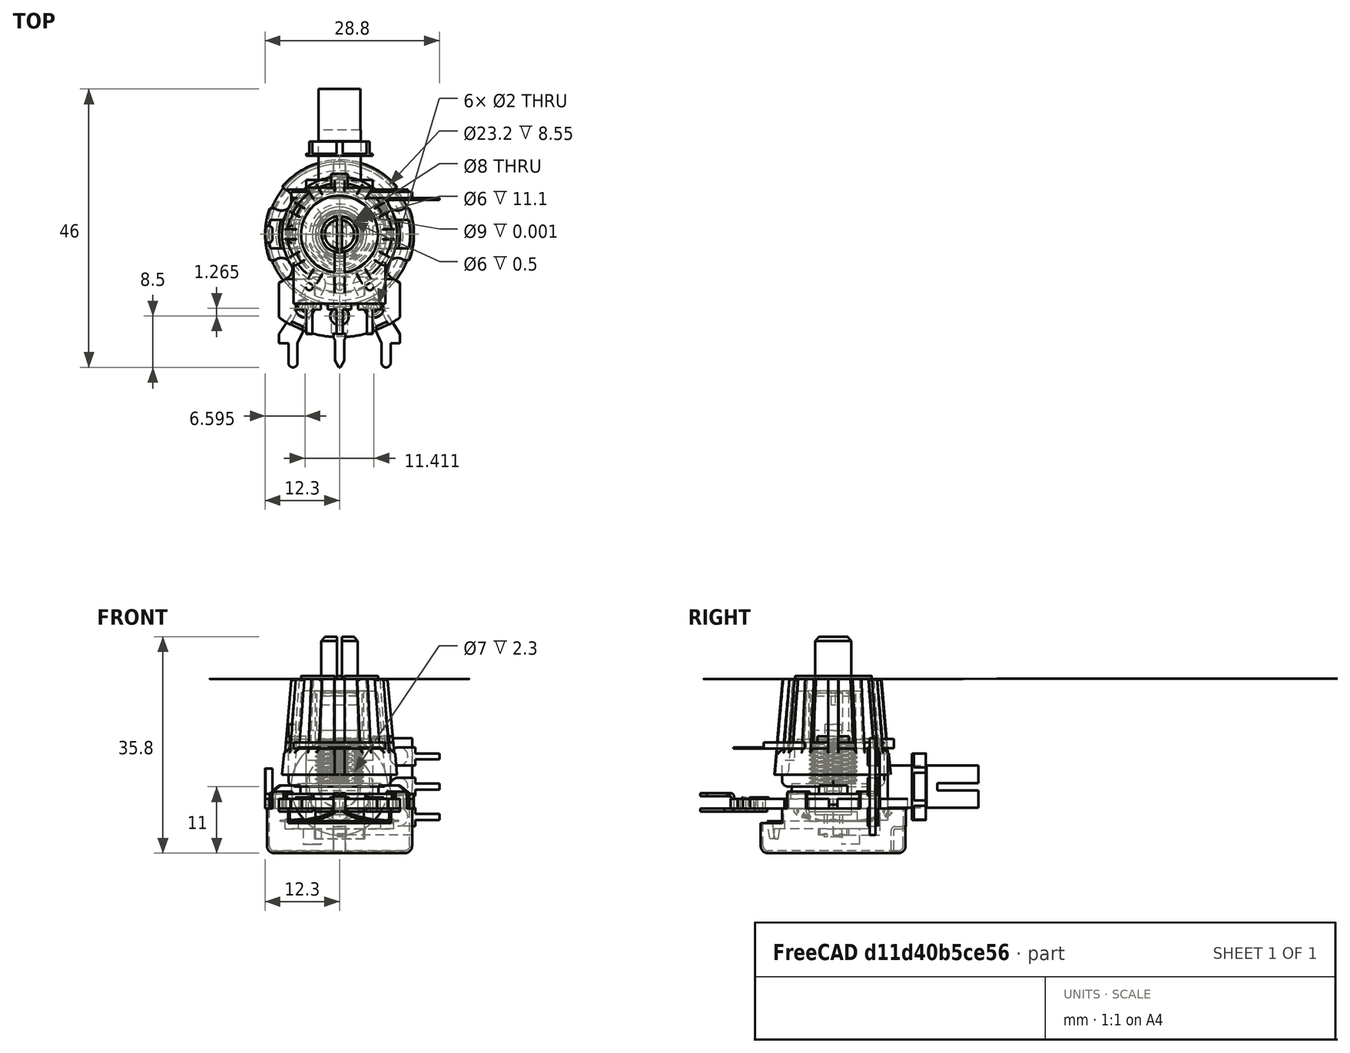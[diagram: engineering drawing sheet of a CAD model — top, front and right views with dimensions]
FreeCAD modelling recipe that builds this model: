
FCSTD DOCUMENT  (FreeCAD 0.19R24267 +148 (Git))
Label: potar
License: All rights reserved
LicenseURL: http://en.wikipedia.org/wiki/All_rights_reserved
objects: Part::Feature×7, App::Part×3, Sketcher::SketchObject×3, PartDesign::Body×2, Spreadsheet::Sheet×1, PartDesign::ShapeBinder×1, PartDesign::Pad×1
note: 15 computed .brp shape members not serialized (recipe doc carries the construction recipe); baked Part::Feature solids carry a one-line shape summary decoded from their .brp

FEATURE [Part::Feature] Part__Feature  label="Rotary top"
  shape: bbox 7 x 8.7 x 7 mm, 8 faces (baked)
FEATURE [Part::Feature] Part__Feature001  label="Nut and washer"
  Placement = pos=(0,4,0) rot=(0,0,1;0rad)
  shape: bbox 11 x 2.3 x 11 mm, 16 faces (baked)
FEATURE [Part::Feature] Part__Feature002  label="COMPOUND"
  shape: bbox 24.5 x 15.3 x 16 mm, 54 faces, 6 solids (baked)
FEATURE [Part::Feature] Part__Feature003  label="COMPOUND001"
  shape: bbox 8.7 x 5.6 x 10.5 mm, 0 faces, 0 solids (baked)
FEATURE [Part::Feature] Part__Feature004  label="COMPOUND002"
  shape: bbox 17.4 x 24.95 x 24.8 mm, 138 faces, 12 solids (baked)
FEATURE [App::Part] Document
  Group = -> [Part__Feature003,Part__Feature004]
  Origin = -> Origin002
FEATURE [Part::Feature] Part__Feature005  label="RV24AF-22-15R v16"
  Placement = pos=(0,0,-11) rot=(0,0,-1;1.5708rad)
  shape: bbox 26 x 34.96 x 26.52 mm, 391 faces, 11 solids (baked)
FEATURE [Spreadsheet::Sheet] Spreadsheet  label="potarSp"
  cells = A1=trouDiam; B1(trouDiam)=7; A2=ergotLarg; B2(ergotLarg)=1.5; A3=ergotLong; B3(ergotLong)=2.7; A4=ergotHaut; B4(ergotHaut)=2.3; A5=ergotDistCentre; B5(ergotDistCentre)=6.9; A6=potarJeu; B6(potarJeu)=0.5
FEATURE [Part::Feature] Part__Feature006  label="Turn knob"
  Placement = pos=(0,0,2) rot=(1,0,0;1.5708rad)
  shape: bbox 20.56 x 20.51 x 16.3 mm, 597 faces (baked)
FEATURE [Sketcher::SketchObject] Sketch  label="priseDeCoteDiam"
  FullyConstrained = false
  MapMode = 5
  Support = -> [XY_Plane003]
  sketch-geometry (5):
    g0: Circle CenterX=0 CenterY=0 CenterZ=0 NormalX=0 NormalY=0 NormalZ=1 AngleXU=0 Radius=8.02
    g1: LineSegment StartX=-1.42985 StartY=-6.8 StartZ=0 EndX=1.24463 EndY=-6.8 EndZ=0
    g2: LineSegment StartX=1.24463 StartY=-6.8 StartZ=0 EndX=1.24463 EndY=-8.08506 EndZ=0
    g3: LineSegment StartX=1.24463 StartY=-8.08506 StartZ=0 EndX=-1.42985 EndY=-8.08506 EndZ=0
    g4: LineSegment StartX=-1.42985 StartY=-8.08506 StartZ=0 EndX=-1.42985 EndY=-6.8 EndZ=0
  constraints (11):
    c: Coincident(g0,g-1)
    c: Diameter(g0) = 16.04
    c: Coincident(g1,g2)
    c: Coincident(g2,g3)
    c: Coincident(g3,g4)
    c: Coincident(g4,g1)
    c: Horizontal(g1)
    c: Horizontal(g3)
    c: Vertical(g2)
    c: Vertical(g4)
    c: DistanceY(g1,g0) = 6.8
FEATURE [Sketcher::SketchObject] Sketch001  label="prisesDeDimension"
  FullyConstrained = false
  MapMode = 5
  Placement = pos=(0,0,0) rot=(0.57735,0.57735,0.57735;2.0944rad)
  Support = -> [YZ_Plane003]
  sketch-geometry (16):
    g0: LineSegment StartX=-7.8626 StartY=-3.32803 StartZ=0 EndX=8.0374 EndY=-3.32803 EndZ=0
    g1: LineSegment StartX=8.0374 StartY=-3.32803 StartZ=0 EndX=8.0374 EndY=-9.32803 EndZ=0
    g2: LineSegment StartX=8.0374 StartY=-9.32803 StartZ=0 EndX=-7.8626 EndY=-9.32803 EndZ=0
    g3: LineSegment StartX=-7.8626 StartY=-9.32803 StartZ=0 EndX=-7.8626 EndY=-3.32803 EndZ=0
    g4: LineSegment StartX=-12.0374 StartY=-2.15213 StartZ=0 EndX=7.91511 EndY=-2.15213 EndZ=0
    g5: LineSegment StartX=7.91511 StartY=-2.15213 StartZ=0 EndX=7.91511 EndY=-3.14213 EndZ=0
    g6: LineSegment StartX=7.91511 StartY=-3.14213 StartZ=0 EndX=-12.0374 EndY=-3.14213 EndZ=0
    g7: LineSegment StartX=-12.0374 StartY=-3.14213 StartZ=0 EndX=-12.0374 EndY=-2.15213 EndZ=0
    g8: LineSegment StartX=-5.52233 StartY=-0.212131 StartZ=0 EndX=5.45051 EndY=-0.212131 EndZ=0
    g9: LineSegment StartX=5.45051 StartY=-0.212131 StartZ=0 EndX=5.45051 EndY=-2.15213 EndZ=0
    g10: LineSegment StartX=5.45051 StartY=-2.15213 StartZ=0 EndX=-5.52233 EndY=-2.15213 EndZ=0
    g11: LineSegment StartX=-5.52233 StartY=-2.15213 StartZ=0 EndX=-5.52233 EndY=-0.212131 EndZ=0
    g12: LineSegment StartX=-5.45036 StartY=3.77787 StartZ=0 EndX=5.45051 EndY=3.77787 EndZ=0
    g13: LineSegment StartX=5.45051 StartY=3.77787 StartZ=0 EndX=5.45051 EndY=-0.212131 EndZ=0
    g14: LineSegment StartX=5.45051 StartY=-0.212131 StartZ=0 EndX=-5.45036 EndY=-0.212131 EndZ=0
    g15: LineSegment StartX=-5.45036 StartY=-0.212131 StartZ=0 EndX=-5.45036 EndY=3.77787 EndZ=0
  constraints (39):
    c: Coincident(g0,g1)
    c: Coincident(g1,g2)
    c: Coincident(g2,g3)
    c: Coincident(g3,g0)
    c: Horizontal(g0)
    c: Horizontal(g2)
    c: Vertical(g1)
    c: Vertical(g3)
    c: DistanceX(g2,g2) = 15.9
    c: DistanceY(g1,g1) = 6
    c: Coincident(g4,g5)
    c: Coincident(g5,g6)
    c: Coincident(g6,g7)
    c: Coincident(g7,g4)
    c: Horizontal(g4)
    c: Horizontal(g6)
    c: Vertical(g5)
    c: Vertical(g7)
    c: DistanceY(g5,g5) = 0.99
    c: Coincident(g8,g9)
    c: Coincident(g9,g10)
    c: Coincident(g10,g11)
    c: Coincident(g11,g8)
    c: Horizontal(g8)
    c: Horizontal(g10)
    c: Vertical(g9)
    c: Vertical(g11)
    c: PointOnObject(g9,g4)
    c: DistanceY(g9,g9) = 1.94
    c: Coincident(g12,g13)
    c: Coincident(g13,g14)
    c: Coincident(g14,g15)
    c: Coincident(g15,g12)
    c: Horizontal(g12)
    c: Horizontal(g14)
    c: Vertical(g13)
    c: Vertical(g15)
    c: Coincident(g13,g8)
    c: DistanceY(g13,g13) = 3.99
FEATURE [PartDesign::Body] Body
  Group = -> [Sketch,Sketch001]
  Origin = -> Origin003
FEATURE [PartDesign::ShapeBinder] ReferencePart__Feature002
  Support = -> [Part__Feature002]
  TraceSupport = false
FEATURE [Sketcher::SketchObject] Sketch002
  ExternalGeometry = -> [ReferencePart__Feature002]
  FullyConstrained = true
  MapMode = 5
  Placement = pos=(0,7.7,0) rot=(0,0.707107,0.707107;3.14159rad)
  Support = -> [ReferencePart__Feature002]
  expr: Constraints[10] = <<potarSp>>.ergotLong
  expr: Constraints[9] = <<potarSp>>.ergotLarg
  sketch-geometry (4):
    g0: LineSegment StartX=-1.35 StartY=7.88527 StartZ=0 EndX=1.35 EndY=7.88527 EndZ=0
    g1: LineSegment StartX=1.35 StartY=7.88527 StartZ=0 EndX=1.35 EndY=6.38527 EndZ=0
    g2: LineSegment StartX=1.35 StartY=6.38527 StartZ=0 EndX=-1.35 EndY=6.38527 EndZ=0
    g3: LineSegment StartX=-1.35 StartY=6.38527 StartZ=0 EndX=-1.35 EndY=7.88527 EndZ=0
  constraints (11):
    c: Coincident(g0,g1)
    c: Coincident(g1,g2)
    c: Coincident(g2,g3)
    c: Coincident(g3,g0)
    c: Horizontal(g2)
    c: Vertical(g1)
    c: Vertical(g3)
    c: Symmetric(g0,g0,g-2)
    c: PointOnObject(g0,g-3)
    c: DistanceY(g1,g1) = 1.5
    c: DistanceX(g2,g2) = 2.7
FEATURE [PartDesign::Pad] Pad
  Direction = (1,1,1)
  Length = 2.3
  Length2 = 100
  Profile = -> Sketch002
  Type = 0
  expr: Length = <<potarSp>>.ergotHaut
FEATURE [PartDesign::Body] Body001
  Group = -> [ReferencePart__Feature002,Sketch002,Pad]
  Origin = -> Origin004
  Tip = -> Pad
FEATURE [App::Part] Potentiometer_v7  label="Potentiometer v7"
  Group = -> [Part__Feature,Part__Feature001,Part__Feature002,Body001]
  Origin = -> Origin
  Placement = pos=(-2.1e-15,6e-15,-9) rot=(1,0,0;1.5708rad)
FEATURE [App::Part] Part  label="potarPart"
  Group = -> [Potentiometer_v7,Document,Part__Feature005,Spreadsheet,Part__Feature006,Body]
  Origin = -> Origin001
